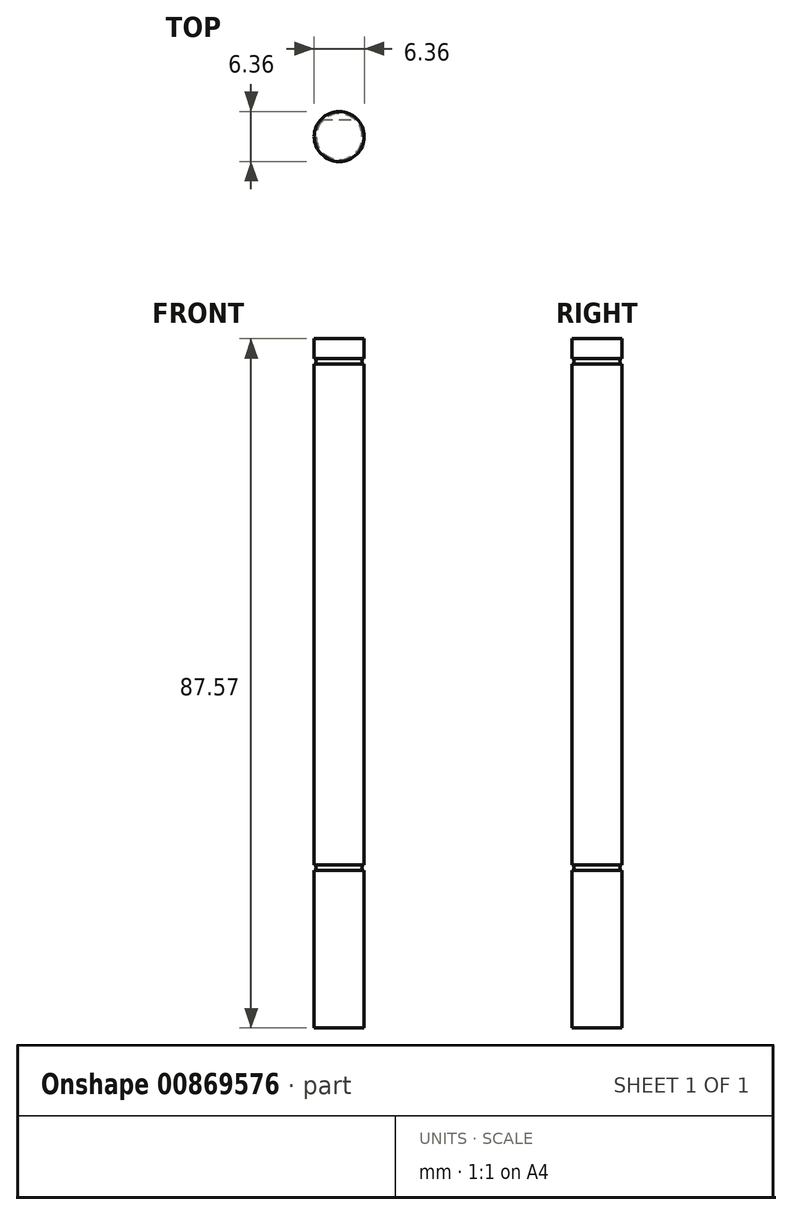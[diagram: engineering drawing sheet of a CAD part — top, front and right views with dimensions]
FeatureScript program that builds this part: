
annotation { "Feature Type Name" : "Feature", "Feature Type Description" : "" }
export const myFeature = defineFeature(function(context is Context, id is Id, definition is map)
    precondition{}
    {
        {
            var Q0;
            Q0=qCreatedBy(makeId("Top.planeOp"),FACE);
            var sketch = newSketch(context, id + "F0", { "sketchPlane" : qUnion([Q0])});
            skCircle(sketch, "E0", {"center": v(0, 0) * mm, "radius": 3.18 * mm});
            skSolve(sketch);
        }
        {
            var Q0;
            Q0 = qSketchRegion(id + "F0", true);
            extrude(context, id + "F1", {"entities" : qUnion([Q0]), "flatOperationType" : FlatOperationType.REMOVE, "depth" : (90 - 2.8) * mm + 0.36 * mm, "offsetDistance" : 25 * mm, "domain" : OperationDomain.MODEL});
        }
        {
            var Q0;
            Q0=makeQuery(id+"F1.opExtrude","CAP_FACE",FACE,{"disambiguationData":[OSD([sQuery(id+"F0.wireOp",EDGE,"E0")])],"isStart":true});
            cPlane(context, id + "F2", {"entities" : qUnion([Q0]), "cplaneType" : CPlaneType.OFFSET, "offset" : 20 * mm, "oppositeDirection" : true, "width" : 150 * mm, "height" : 150 * mm});
        }
        {
            var Q0;
            Q0=qCreatedBy(id+"F2.planeOp",FACE);
            var sketch = newSketch(context, id + "F3", { "sketchPlane" : qUnion([Q0])});
            skCircle(sketch, "E1", {"center": v(0, 0) * mm, "radius": 3.18 * mm});
            skCircle(sketch, "E2", {"center": v(0, 0) * mm, "radius": 2.92 * mm});
            skSolve(sketch);
        }
        {
            var Q0;
            Q0 = qSketchRegion(id + "F3", true);
            extrude(context, id + "F4", {"entities" : qUnion([Q0]), "operationType" : NewBodyOperationType.REMOVE, "oppositeDirection" : true, "depth" : 0.74 * mm, "offsetDistance" : 25 * mm});
        }
        {
            var Q0;
            Q0=qCreatedBy(id+"F2.planeOp",FACE);
            cPlane(context, id + "F5", {"entities" : qUnion([Q0]), "cplaneType" : CPlaneType.OFFSET, "offset" : 63.35 * mm + 0.25 * mm + 0.74 * mm, "oppositeDirection" : true, "width" : 150 * mm, "height" : 150 * mm});
        }
        {
            var Q0;
            Q0=qCreatedBy(id+"F5.planeOp",FACE);
            var sketch = newSketch(context, id + "F6", { "sketchPlane" : qUnion([Q0])});
            skCircle(sketch, "E3", {"center": v(0, 0) * mm, "radius": 3.18 * mm});
            skCircle(sketch, "E4", {"center": v(0, 0) * mm, "radius": 2.92 * mm});
            skSolve(sketch);
        }
        {
            var Q0;
            Q0 = qSketchRegion(id + "F6", true);
            extrude(context, id + "F7", {"entities" : qUnion([Q0]), "operationType" : NewBodyOperationType.REMOVE, "oppositeDirection" : true, "depth" : 0.74 * mm, "offsetDistance" : 25 * mm});
        }
        {
            var Q0;
            Q0=makeQuery(id+"F1.opExtrude","CAP_FACE",FACE,{"disambiguationData":[OSD([sQuery(id+"F0.wireOp",EDGE,"E0")])],"isStart":true});
            var sketch = newSketch(context, id + "F8", { "sketchPlane" : qUnion([Q0])});
            skArc(sketch, "E5", {"start": v(-2.33, -2.16) * mm, "mid": v(0, -3.17) * mm, "end": v(2.33, -2.16) * mm});
            skLineSegment(sketch, "E6", {"start": v(-2.33, -2.16) * mm, "end": v(2.33, -2.16) * mm});
            skSolve(sketch);
        }
        {
            var Q0;
            Q0 = qSketchRegion(id + "F8", true);
            extrude(context, id + "F9", {"entities" : qUnion([Q0]), "operationType" : NewBodyOperationType.REMOVE, "oppositeDirection" : true, "depth" : 1 / 101.6 * mm, "offsetDistance" : 25 * mm});
        }
    });
